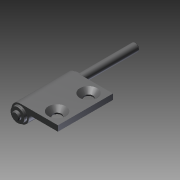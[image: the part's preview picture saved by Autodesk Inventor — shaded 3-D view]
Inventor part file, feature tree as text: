
AUTODESK INVENTOR PART (.ipt)
format: ipt  version: 2011 SP1 (Build 150282100, 282)  size: 130,048 bytes
history: native  units: mm
features: other x35, sketch x4, hole x2, revolve x1, extrude x1
ambient origin geometry x8: Origin, YZ Plane, XZ Plane, XY Plane, X Axis, Y Axis, Z Axis, Center Point
bodies: Solid1 (feature_tree)
feature tree (43):
  revolve  "Revolution1"  [1 undecoded]
  extrude  "Extrusion1"  TaperAngle=0.0deg  [1 undecoded]
  hole  "Hole1"  [1 undecoded]
  hole  "Hole2"  [1 undecoded]
  other  "1_XY"
  other  "1_YZ"
  other  "1_ZX"
  other  "1_X"
  other  "1_Y"
  other  "1_Z"
  other  "1_Center"
  other  "to_bolt1_XY"
  other  "to_bolt1_YZ"
  other  "to_bolt1_ZX"
  other  "to_bolt1_X"
  other  "to_bolt1_Y"
  other  "to_bolt1_Z"
  other  "to_bolt1_Center"
  other  "to_bolt1_r_XY"
  other  "to_bolt1_r_YZ"
  other  "to_bolt1_r_ZX"
  other  "to_bolt1_r_X"
  other  "to_bolt1_r_Y"
  other  "to_bolt1_r_Z"
  other  "to_bolt1_r_Center"
  other  "to_bolt2_XY"
  other  "to_bolt2_YZ"
  other  "to_bolt2_ZX"
  other  "to_bolt2_X"
  other  "to_bolt2_Y"
  other  "to_bolt2_Z"
  other  "to_bolt2_Center"
  other  "to_bolt2_r_XY"
  other  "to_bolt2_r_YZ"
  other  "to_bolt2_r_ZX"
  other  "to_bolt2_r_X"
  other  "to_bolt2_r_Y"
  other  "to_bolt2_r_Z"
  other  "to_bolt2_r_Center"
  sketch  "Sketch_1"  dims[d0=360.0deg d1=3.5mm d2=0.0mm]
  sketch  "Sketch_2"  dims[d3=5.5mm d4=6.0mm d5=11.0mm d6=2.0mm d7=90.0deg d8=3.5mm d9=0.0mm]
  sketch  "Sketch3"  dims[d10=5.5mm d11=6.0mm d12=11.0mm d13=2.0mm d14=90.0deg d15=3.5mm d16=0.0mm d17=0.0mm d18=0.0mm d19=0.0mm]
  sketch  "Sketch4"
note: 4 required parameter values undecoded (feature->parameter linkage not recoverable at this tier; creation-order binding heuristic only, values carry confidence <= 0.55)